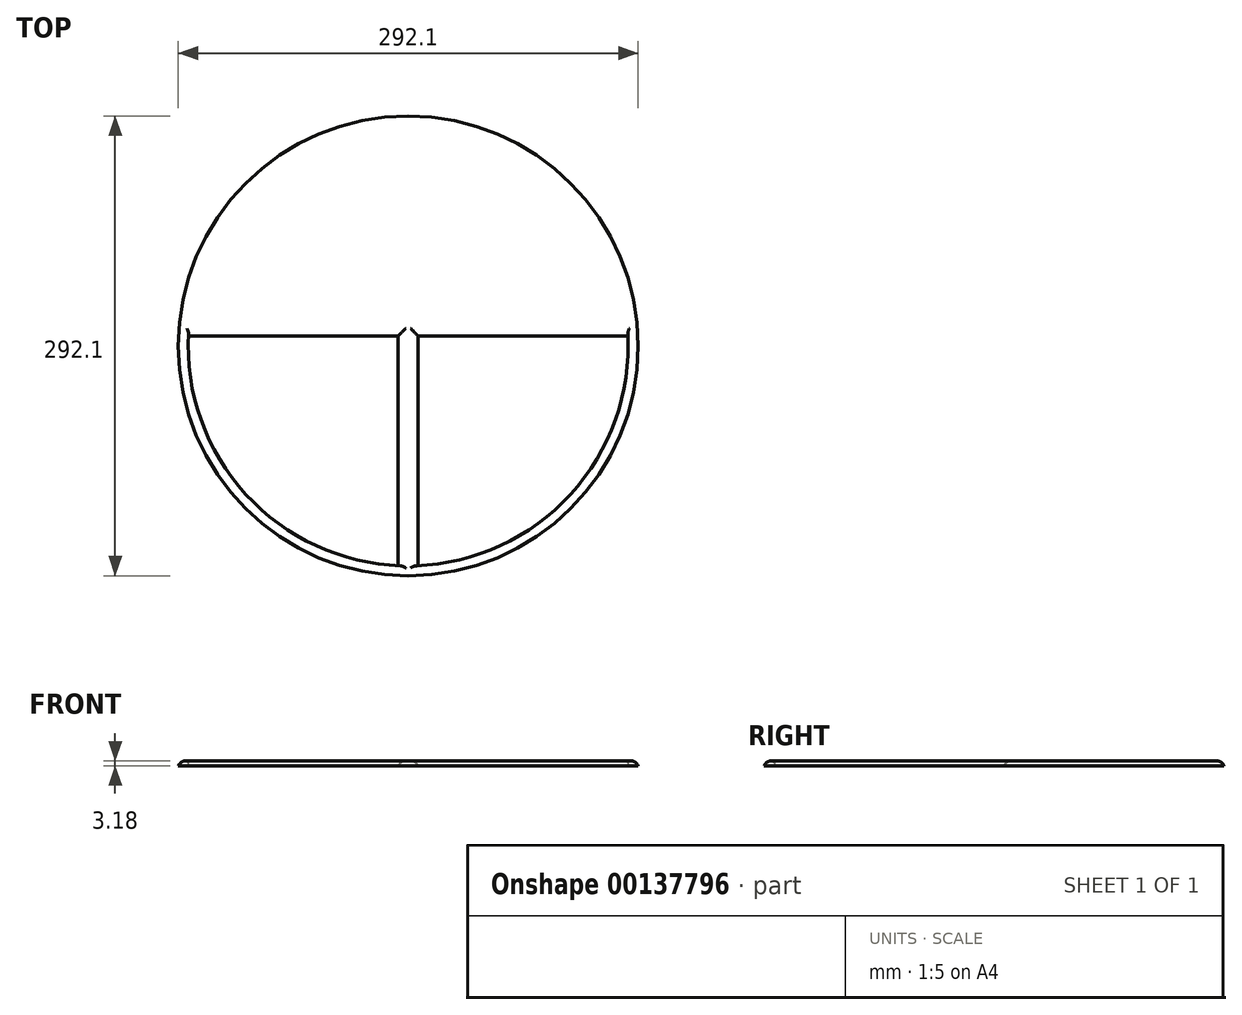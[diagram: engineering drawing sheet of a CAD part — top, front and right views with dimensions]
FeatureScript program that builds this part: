
annotation { "Feature Type Name" : "Feature", "Feature Type Description" : "" }
export const myFeature = defineFeature(function(context is Context, id is Id, definition is map)
    precondition{}
    {
        {
            var Q0;
            Q0=qCreatedBy(makeId("Top.planeOp"),FACE);
            var sketch = newSketch(context, id + "F0", { "sketchPlane" : qUnion([Q0])});
            skCircle(sketch, "E0", {"center": v(0, 0) * mm, "radius": 146.05 * mm});
            skCircle(sketch, "E1", {"center": v(0, 0) * mm, "radius": 139.7 * mm});
            skLineSegment(sketch, "E2", {"start": v(-6.35, 139.56) * mm, "end": v(-6.35, -139.56) * mm});
            skLineSegment(sketch, "E3", {"start": v(6.35, -139.56) * mm, "end": v(6.35, 139.56) * mm});
            skLineSegment(sketch, "E4", {"start": v(-139.56, 6.35) * mm, "end": v(139.56, 6.35) * mm});
            skLineSegment(sketch, "E5", {"start": v(-139.56, -6.35) * mm, "end": v(139.56, -6.35) * mm});
            skSolve(sketch);
        }
        {
            var Q0;
            Q0=makeQuery(id+"F0.imprint","IMPRINT",FACE,{"disambiguationData":[TD([[makeQuery(id+"F0.imprint","IMPRINT",EDGE,{"derivedFrom":sQuery(id+"F0.wireOp",EDGE,"E0")}),1.0]])]});
            var Q1;
            {var subQ0=sQuery(id+"F0.wireOp",EDGE,"E4");var subQ1=sQuery(id+"F0.wireOp",EDGE,"E1");var subQ2=makeQuery(id+"F0.imprint","INTERSECT",VERTEX,{"disambiguationData":[OD(0.0)],"derivedFrom":[subQ1,subQ0]});Q1=makeQuery(id+"F0.imprint","IMPRINT",FACE,{"disambiguationData":[TD([[makeQuery(id+"F0.imprint","IMPRINT",EDGE,{"disambiguationData":[TD([[subQ2,-1.0]])],"derivedFrom":subQ1}),1.0]])]});}
            var Q2;
            {var subQ0=sQuery(id+"F0.wireOp",EDGE,"E2");var subQ1=sQuery(id+"F0.wireOp",EDGE,"E1");var subQ2=makeQuery(id+"F0.imprint","INTERSECT",VERTEX,{"disambiguationData":[OD(0.0)],"derivedFrom":[subQ1,subQ0]});Q2=makeQuery(id+"F0.imprint","IMPRINT",FACE,{"disambiguationData":[TD([[makeQuery(id+"F0.imprint","IMPRINT",EDGE,{"disambiguationData":[TD([[subQ2,1.0]])],"derivedFrom":subQ1}),1.0]])]});}
            var Q3;
            {var subQ0=sQuery(id+"F0.wireOp",EDGE,"E4");var subQ1=sQuery(id+"F0.wireOp",EDGE,"E1");var subQ2=makeQuery(id+"F0.imprint","INTERSECT",VERTEX,{"disambiguationData":[OD(1.0)],"derivedFrom":[subQ1,subQ0]});Q3=makeQuery(id+"F0.imprint","IMPRINT",FACE,{"disambiguationData":[TD([[makeQuery(id+"F0.imprint","IMPRINT",EDGE,{"disambiguationData":[TD([[subQ2,1.0]])],"derivedFrom":subQ1}),1.0]])]});}
            var Q4;
            {var subQ0=sQuery(id+"F0.wireOp",EDGE,"E2");var subQ1=sQuery(id+"F0.wireOp",EDGE,"E1");var subQ2=makeQuery(id+"F0.imprint","INTERSECT",VERTEX,{"disambiguationData":[OD(1.0)],"derivedFrom":[subQ1,subQ0]});Q4=makeQuery(id+"F0.imprint","IMPRINT",FACE,{"disambiguationData":[TD([[makeQuery(id+"F0.imprint","IMPRINT",EDGE,{"disambiguationData":[TD([[subQ2,-1.0]])],"derivedFrom":subQ1}),1.0]])]});}
            var Q5;
            {var subQ0=sQuery(id+"F0.wireOp",EDGE,"E4");var subQ1=sQuery(id+"F0.wireOp",EDGE,"E2");var subQ2=makeQuery(id+"F0.imprint","INTERSECT",VERTEX,{"derivedFrom":[subQ1,subQ0]});Q5=makeQuery(id+"F0.imprint","IMPRINT",FACE,{"disambiguationData":[TD([[makeQuery(id+"F0.imprint","IMPRINT",EDGE,{"disambiguationData":[TD([[subQ2,-1.0]])],"derivedFrom":subQ1}),1.0]])]});}
            extrude(context, id + "F1", {"entities" : qUnion([Q0, Q1, Q2, Q3, Q4, Q5]), "depth" : 3.17 * mm, "offsetDistance" : 25.4 * mm});
        }
        {
            var Q0;
            Q0=makeQuery(id+"F1.opExtrude","CAP_EDGE",EDGE,{"disambiguationData":[OSD([sQuery(id+"F0.wireOp",EDGE,"E0")])],"isStart":false});
            fillet(context, id + "F2", {"entities" : qUnion([Q0]), "radius" : 5.08 * mm, "tangentPropagation" : true, "allowEdgeOverflow" : false});
        }
        {
            var Q0;
            Q0=makeQuery(id+"F1.opExtrude","CAP_EDGE",EDGE,{"disambiguationData":[OSD([sQuery(id+"F0.wireOp",EDGE,"E1")])],"isStart":false});
            fillet(context, id + "F3", {"entities" : qUnion([Q0]), "radius" : 1.27 * mm, "tangentPropagation" : true, "allowEdgeOverflow" : false});
        }
        {
            var Q0;
            {var subQ0=sQuery(id+"F0.wireOp",EDGE,"E5");Q0=makeQuery(id+"F1.opExtrude","CAP_EDGE",EDGE,{"disambiguationData":[OSD([subQ0]),TDD([makeQuery(id+"F0.imprint","IMPRINT",EDGE,{"disambiguationData":[TD([[makeQuery(id+"F0.imprint","INTERSECT",VERTEX,{"disambiguationData":[OD(0.0)],"derivedFrom":[sQuery(id+"F0.wireOp",EDGE,"E1"),subQ0]}),-1.0]])],"derivedFrom":subQ0})])],"isStart":false});}
            var Q1;
            {var subQ0=sQuery(id+"F0.wireOp",EDGE,"E5");Q1=makeQuery(id+"F1.opExtrude","CAP_EDGE",EDGE,{"disambiguationData":[OSD([subQ0]),TDD([makeQuery(id+"F0.imprint","IMPRINT",EDGE,{"disambiguationData":[TD([[makeQuery(id+"F0.imprint","INTERSECT",VERTEX,{"disambiguationData":[OD(1.0)],"derivedFrom":[sQuery(id+"F0.wireOp",EDGE,"E1"),subQ0]}),1.0]])],"derivedFrom":subQ0})])],"isStart":false});}
            var Q2;
            {var subQ0=sQuery(id+"F0.wireOp",EDGE,"E3");Q2=makeQuery(id+"F1.opExtrude","CAP_EDGE",EDGE,{"disambiguationData":[OSD([subQ0]),TDD([makeQuery(id+"F0.imprint","IMPRINT",EDGE,{"disambiguationData":[TD([[makeQuery(id+"F0.imprint","INTERSECT",VERTEX,{"disambiguationData":[OD(0.0)],"derivedFrom":[sQuery(id+"F0.wireOp",EDGE,"E1"),subQ0]}),-1.0]])],"derivedFrom":subQ0})])],"isStart":false});}
            var Q3;
            {var subQ0=sQuery(id+"F0.wireOp",EDGE,"E2");Q3=makeQuery(id+"F1.opExtrude","CAP_EDGE",EDGE,{"disambiguationData":[OSD([subQ0]),TDD([makeQuery(id+"F0.imprint","IMPRINT",EDGE,{"disambiguationData":[TD([[makeQuery(id+"F0.imprint","INTERSECT",VERTEX,{"disambiguationData":[OD(1.0)],"derivedFrom":[sQuery(id+"F0.wireOp",EDGE,"E1"),subQ0]}),1.0]])],"derivedFrom":subQ0})])],"isStart":false});}
            var Q4;
            {var subQ0=sQuery(id+"F0.wireOp",EDGE,"E2");Q4=makeQuery(id+"F1.opExtrude","CAP_EDGE",EDGE,{"disambiguationData":[OSD([subQ0]),TDD([makeQuery(id+"F0.imprint","IMPRINT",EDGE,{"disambiguationData":[TD([[makeQuery(id+"F0.imprint","INTERSECT",VERTEX,{"disambiguationData":[OD(0.0)],"derivedFrom":[sQuery(id+"F0.wireOp",EDGE,"E1"),subQ0]}),-1.0]])],"derivedFrom":subQ0})])],"isStart":false});}
            var Q5;
            {var subQ0=sQuery(id+"F0.wireOp",EDGE,"E4");Q5=makeQuery(id+"F1.opExtrude","CAP_EDGE",EDGE,{"disambiguationData":[OSD([subQ0]),TDD([makeQuery(id+"F0.imprint","IMPRINT",EDGE,{"disambiguationData":[TD([[makeQuery(id+"F0.imprint","INTERSECT",VERTEX,{"disambiguationData":[OD(0.0)],"derivedFrom":[sQuery(id+"F0.wireOp",EDGE,"E1"),subQ0]}),-1.0]])],"derivedFrom":subQ0})])],"isStart":false});}
            var Q6;
            {var subQ0=sQuery(id+"F0.wireOp",EDGE,"E3");Q6=makeQuery(id+"F1.opExtrude","CAP_EDGE",EDGE,{"disambiguationData":[OSD([subQ0]),TDD([makeQuery(id+"F0.imprint","IMPRINT",EDGE,{"disambiguationData":[TD([[makeQuery(id+"F0.imprint","INTERSECT",VERTEX,{"disambiguationData":[OD(1.0)],"derivedFrom":[sQuery(id+"F0.wireOp",EDGE,"E1"),subQ0]}),1.0]])],"derivedFrom":subQ0})])],"isStart":false});}
            var Q7;
            Q7=makeQuery(id+"F1.opExtrude","CAP_FACE",FACE,{"disambiguationData":[OSD([sQuery(id+"F0.wireOp",EDGE,"E0"),sQuery(id+"F0.wireOp",EDGE,"E1"),sQuery(id+"F0.wireOp",EDGE,"E2"),sQuery(id+"F0.wireOp",EDGE,"E3"),sQuery(id+"F0.wireOp",EDGE,"E4"),sQuery(id+"F0.wireOp",EDGE,"E5")])],"isStart":false});
            fillet(context, id + "F4", {"entities" : qUnion([Q0, Q1, Q2, Q3, Q4, Q5, Q6, Q7]), "radius" : 5.33 * mm, "tangentPropagation" : true, "allowEdgeOverflow" : false});
        }
    });
